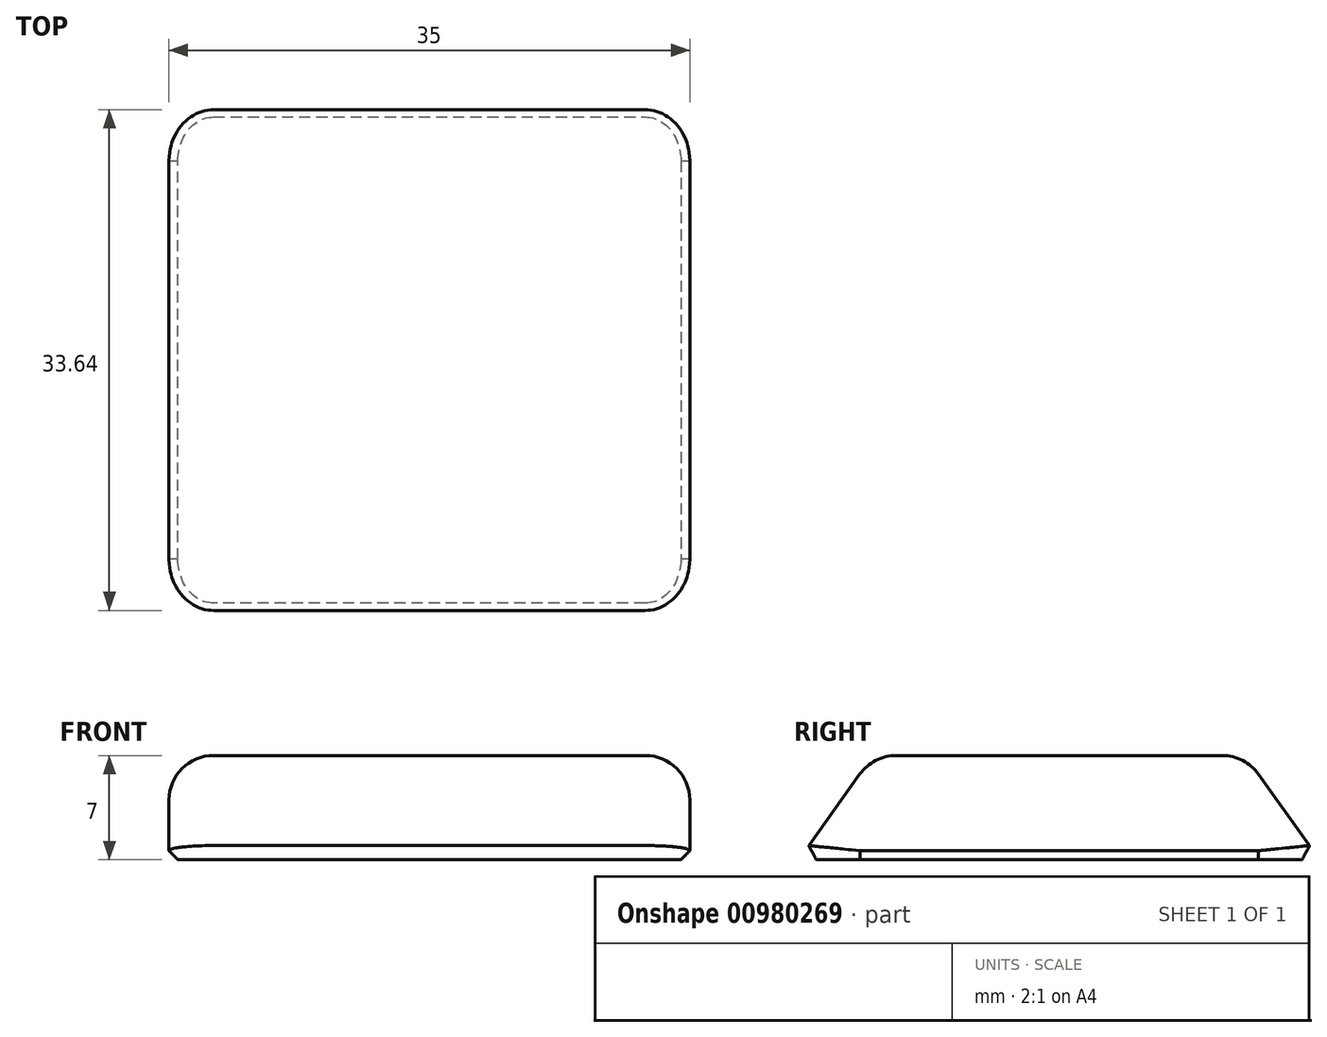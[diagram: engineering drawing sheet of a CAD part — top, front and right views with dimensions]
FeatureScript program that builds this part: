
annotation { "Feature Type Name" : "Feature", "Feature Type Description" : "" }
export const myFeature = defineFeature(function(context is Context, id is Id, definition is map)
    precondition{}
    {
        {
            var Q0;
            Q0=qCreatedBy(makeId("Right.planeOp"),FACE);
            var sketch = newSketch(context, id + "F0", { "sketchPlane" : qUnion([Q0])});
            skLineSegment(sketch, "E0", {"start": v(-17.5, 0) * mm, "end": v(-12.5, 7) * mm});
            skLineSegment(sketch, "E1", {"start": v(-12.5, 7) * mm, "end": v(12.5, 7) * mm});
            skLineSegment(sketch, "E2", {"start": v(12.5, 7) * mm, "end": v(17.5, 0) * mm});
            skLineSegment(sketch, "E3", {"start": v(17.5, 0) * mm, "end": v(-17.5, 0) * mm});
            skPoint(sketch, "E4", {"position": v(0, 7) * mm});
            skSolve(sketch);
        }
        {
            var Q0;
            Q0=makeQuery(id+"F0.imprint","IMPRINT",FACE,{"disambiguationData":[TD([[makeQuery(id+"F0.imprint","IMPRINT",EDGE,{"derivedFrom":sQuery(id+"F0.wireOp",EDGE,"E0")}),-1.0]])]});
            extrude(context, id + "F1", {"entities" : qUnion([Q0]), "depth" : 35 * mm, "offsetDistance" : 25 * mm});
        }
        {
            var Q0;
            Q0=makeQuery(id+"F1.opExtrude","SWEPT_EDGE",EDGE,{"disambiguationData":[OSD([sQuery(id+"F0.wireOp",EDGE,"E1"),sQuery(id+"F0.wireOp",EDGE,"E2")])]});
            var Q1;
            Q1=makeQuery(id+"F1.opExtrude","SWEPT_FACE",FACE,{"disambiguationData":[OSD([sQuery(id+"F0.wireOp",EDGE,"E1")])]});
            var Q2;
            Q2=makeQuery(id+"F1.opExtrude","CAP_EDGE",EDGE,{"disambiguationData":[OSD([sQuery(id+"F0.wireOp",EDGE,"E2")])],"isStart":false});
            var Q3;
            Q3=makeQuery(id+"F1.opExtrude","CAP_EDGE",EDGE,{"disambiguationData":[OSD([sQuery(id+"F0.wireOp",EDGE,"E2")])],"isStart":true});
            var Q4;
            Q4=makeQuery(id+"F1.opExtrude","CAP_EDGE",EDGE,{"disambiguationData":[OSD([sQuery(id+"F0.wireOp",EDGE,"E0")])],"isStart":true});
            var Q5;
            Q5=makeQuery(id+"F1.opExtrude","CAP_EDGE",EDGE,{"disambiguationData":[OSD([sQuery(id+"F0.wireOp",EDGE,"E0")])],"isStart":false});
            fillet(context, id + "F2", {"entities" : qUnion([Q0, Q1, Q2, Q3, Q4, Q5]), "tangentPropagation" : true, "radius" : 3 * mm, "defaultsChanged" : true, "vertexSettings" : [], "allowEdgeOverflow" : false});
        }
        {
            var Q0;
            Q0=makeQuery(id+"F1.opExtrude","SWEPT_FACE",FACE,{"disambiguationData":[OSD([sQuery(id+"F0.wireOp",EDGE,"E3")])]});
            chamfer(context, id + "F3", {"entities" : qUnion([Q0]), "width" : 0.6 * mm, "tangentPropagation" : true});
        }
    });
